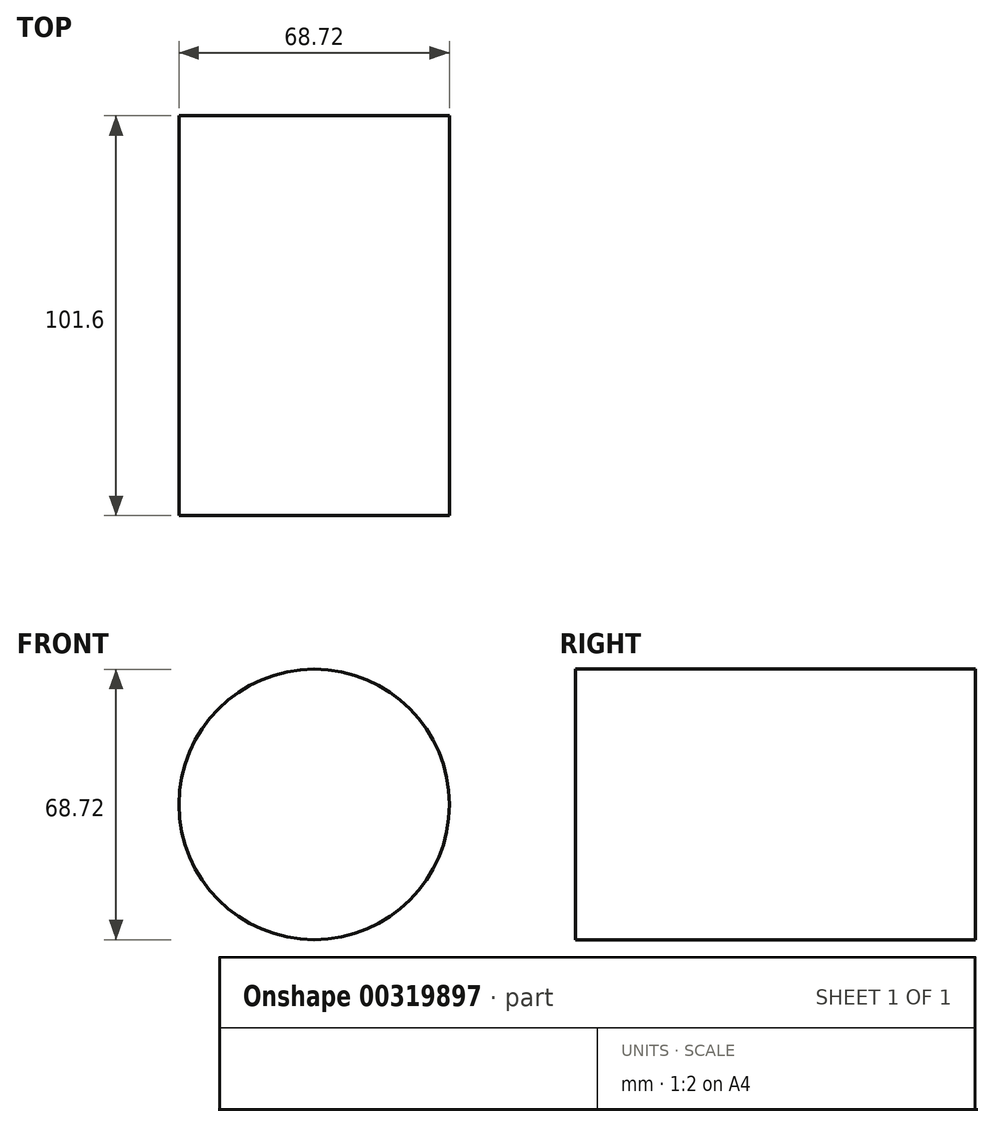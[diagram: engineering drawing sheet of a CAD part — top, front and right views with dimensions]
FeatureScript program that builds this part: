
annotation { "Feature Type Name" : "Feature", "Feature Type Description" : "" }
export const myFeature = defineFeature(function(context is Context, id is Id, definition is map)
    precondition{}
    {
        {
            var Q0;
            Q0=qCreatedBy(makeId("Front.planeOp"),FACE);
            var sketch = newSketch(context, id + "F0", { "sketchPlane" : qUnion([Q0])});
            skCircle(sketch, "E0", {"center": v(0, 0) * mm, "radius": 34.36 * mm});
            skSolve(sketch);
        }
        {
            var Q0;
            Q0 = qSketchRegion(id + "F0", true);
            extrude(context, id + "F1", {"entities" : qUnion([Q0]), "depth" : 101.6 * mm});
        }
    });
